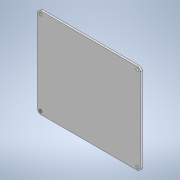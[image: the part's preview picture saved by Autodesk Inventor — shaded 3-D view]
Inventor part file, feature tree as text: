
AUTODESK INVENTOR PART (.ipt)
format: ipt  version: 2020 (Build 240168000, 168)  size: 126,976 bytes
history: native  units: mm
features: other x3, extrude x2, sketch x2, plane x1, reference x1, projected_geometry x1
ambient origin geometry x8: Origin, YZ Plane, XZ Plane, XY Plane, X Axis, Y Axis, Z Axis, Center Point
bodies: 实体1 (feature_tree)
feature tree (10):
  plane  "工作平面1"
  extrude  "拉伸1"  Depth=4.0mm
  extrude  "拉伸2"  Depth=4.0mm
  sketch  "草图1"  dims[d0=4.0mm d1=0.0mm d2=0.5mm]
  reference  "参考1"
  sketch  "草图2"  dims[d3=0.5mm d4=0.5mm d5=0.5mm d6=4.0mm d7=0.0mm]
  projected_geometry  "投影回路1"
  other  "<userpath>\Desktop\ME_course_project\课设试试\shaft_try_1.iam"
  other  "shaft_try_1.iam"
  other  "shang(1):1"
